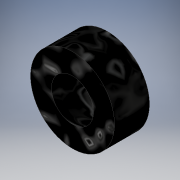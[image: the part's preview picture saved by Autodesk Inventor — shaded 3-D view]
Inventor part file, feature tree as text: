
AUTODESK INVENTOR PART (.ipt)
format: ipt  version: 2019.4 (Build 234330000, 330)  size: 105,472 bytes
history: native  units: mm
features: extrude x1, sketch x1
ambient origin geometry x8: Origin, YZ Plane, XZ Plane, XY Plane, X Axis, Y Axis, Z Axis, Center Point
bodies: Solid1 (feature_tree)
feature tree (2):
  extrude  "Extrusion1"  Depth=12.0mm
  sketch  "Sketch1"  dims[d0=24.0mm d1=12.0mm d2=10.0mm d3=0.0mm]
